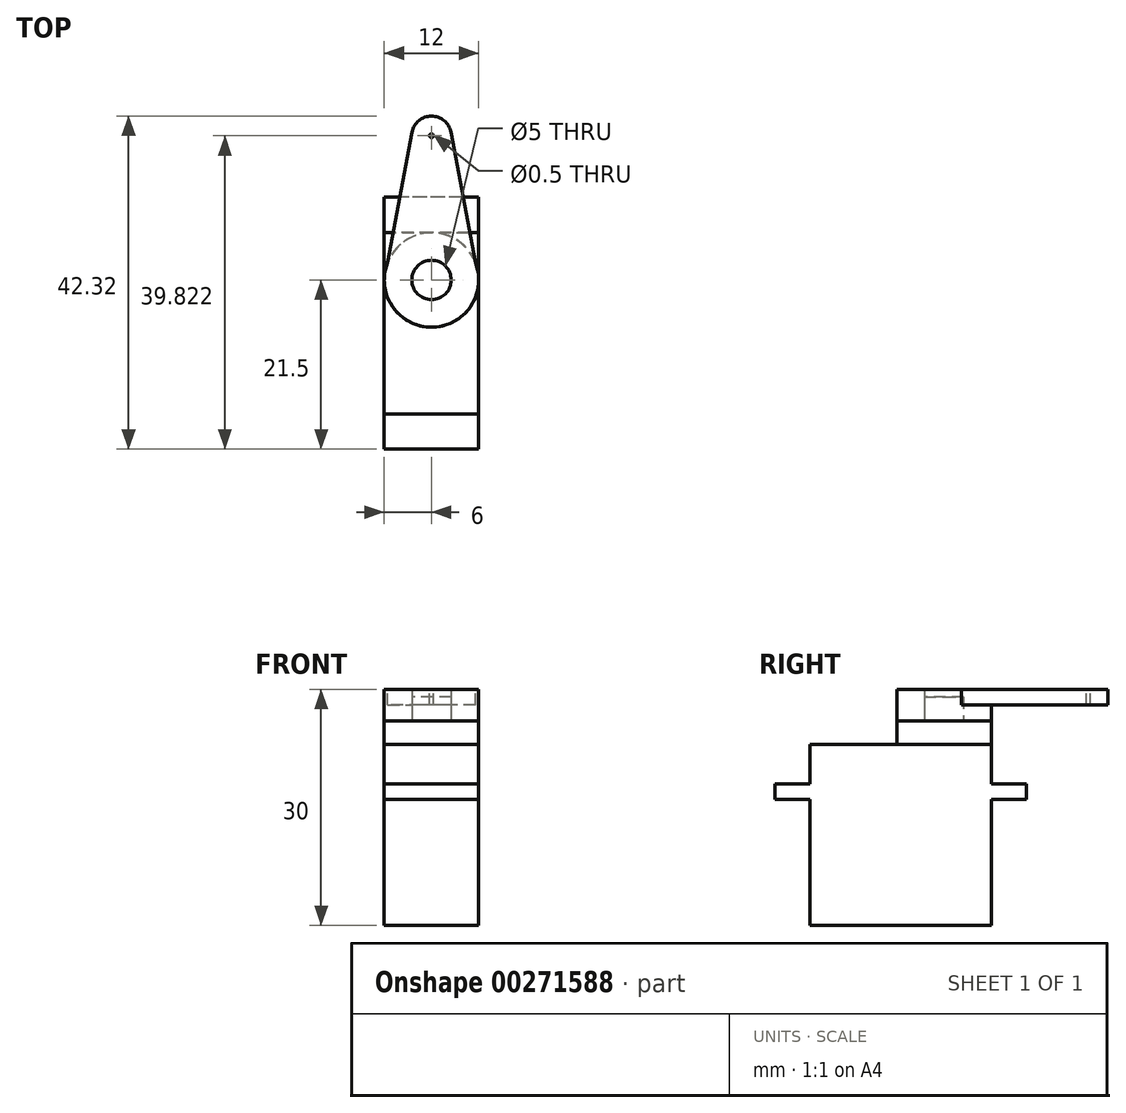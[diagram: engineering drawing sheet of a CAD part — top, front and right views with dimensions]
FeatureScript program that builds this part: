
annotation { "Feature Type Name" : "Feature", "Feature Type Description" : "" }
export const myFeature = defineFeature(function(context is Context, id is Id, definition is map)
    precondition{}
    {
        {
            var Q0;
            Q0=qCreatedBy(makeId("Top.planeOp"),FACE);
            var sketch = newSketch(context, id + "F0", { "sketchPlane" : qUnion([Q0])});
            skLineSegment(sketch, "E0.bottom", {"start": v(6, -16) * mm, "end": v(-6, -16) * mm});
            skLineSegment(sketch, "E0.top", {"start": v(6, 16) * mm, "end": v(-6, 16) * mm});
            skLineSegment(sketch, "E0.left", {"start": v(6, -16) * mm, "end": v(6, 16) * mm});
            skLineSegment(sketch, "E0.right", {"start": v(-6, -16) * mm, "end": v(-6, 16) * mm});
            skPoint(sketch, "E0.middle", {"position": v(0, 0) * mm});
            skSolve(sketch);
        }
        {
            var Q0;
            Q0 = qSketchRegion(id + "F0", true);
            extrude(context, id + "F1", {"entities" : qUnion([Q0]), "depth" : 2 * mm});
        }
        {
            var Q0;
            Q0=makeQuery(id+"F1.opExtrude","CAP_FACE",FACE,{"disambiguationData":[OSD([sQuery(id+"F0.wireOp",EDGE,"E0.bottom"),sQuery(id+"F0.wireOp",EDGE,"E0.top"),sQuery(id+"F0.wireOp",EDGE,"E0.left"),sQuery(id+"F0.wireOp",EDGE,"E0.right")])],"isStart":false});
            var sketch = newSketch(context, id + "F2", { "sketchPlane" : qUnion([Q0])});
            skLineSegment(sketch, "E1.bottom", {"start": v(6, -11.5) * mm, "end": v(-6, -11.5) * mm});
            skLineSegment(sketch, "E1.top", {"start": v(6, 11.5) * mm, "end": v(-6, 11.5) * mm});
            skLineSegment(sketch, "E1.left", {"start": v(6, -11.5) * mm, "end": v(6, 11.5) * mm});
            skLineSegment(sketch, "E1.right", {"start": v(-6, -11.5) * mm, "end": v(-6, 11.5) * mm});
            skPoint(sketch, "E1.middle", {"position": v(0, 0) * mm});
            skSolve(sketch);
        }
        {
            var Q0;
            Q0 = qSketchRegion(id + "F2", true);
            extrude(context, id + "F3", {"entities" : qUnion([Q0]), "operationType" : NewBodyOperationType.ADD, "depth" : 5 * mm, "hasSecondDirection" : true, "secondDirectionOppositeDirection" : true, "secondDirectionDepth" : 18 * mm});
        }
        {
            var Q0;
            Q0=makeQuery(id+"F3.opExtrude","CAP_FACE",FACE,{"disambiguationData":[OSD([sQuery(id+"F2.wireOp",EDGE,"E1.bottom"),sQuery(id+"F2.wireOp",EDGE,"E1.top"),sQuery(id+"F2.wireOp",EDGE,"E1.left"),sQuery(id+"F2.wireOp",EDGE,"E1.right")])],"isStart":false});
            var sketch = newSketch(context, id + "F4", { "sketchPlane" : qUnion([Q0])});
            skCircle(sketch, "E2", {"center": v(0, 5.5) * mm, "radius": 6 * mm});
            skPoint(sketch, "E3", {"position": v(0, 11.5) * mm});
            skSolve(sketch);
        }
        {
            var Q0;
            {var subQ0=sQuery(id+"F4.wireOp",EDGE,"E2");var subQ1=makeQuery(id+"F4.imprint","INTERSECT",VERTEX,{"derivedFrom":[makeQuery(id+"F3.opExtrude","CAP_EDGE",EDGE,{"disambiguationData":[OSD([sQuery(id+"F2.wireOp",EDGE,"E1.top")])],"isStart":false}),subQ0]});Q0=makeQuery(id+"F4.imprint","IMPRINT",FACE,{"disambiguationData":[TD([[makeQuery(id+"F4.imprint","IMPRINT",EDGE,{"disambiguationData":[TD([[subQ1,1.0]])],"derivedFrom":subQ0}),1.0]])]});}
            extrude(context, id + "F5", {"entities" : qUnion([Q0]), "operationType" : NewBodyOperationType.ADD, "depth" : 3 * mm});
        }
        {
            var Q0;
            Q0=makeQuery(id+"F5.opExtrude","CAP_FACE",FACE,{"disambiguationData":[OSD([sQuery(id+"F4.wireOp",EDGE,"E2")])],"isStart":false});
            var sketch = newSketch(context, id + "F6", { "sketchPlane" : qUnion([Q0])});
            skCircle(sketch, "E4", {"center": v(0, 5.5) * mm, "radius": 2.5 * mm});
            skSolve(sketch);
        }
        {
            var Q0;
            Q0 = qSketchRegion(id + "F6", true);
            extrude(context, id + "F7", {"entities" : qUnion([Q0]), "operationType" : NewBodyOperationType.ADD, "depth" : 3 * mm});
        }
        {
            var Q0;
            Q0=makeQuery(id+"F5.opExtrude","CAP_FACE",FACE,{"disambiguationData":[OSD([sQuery(id+"F4.wireOp",EDGE,"E2")])],"isStart":false});
            extrude(context, id + "F8", {"entities" : qUnion([Q0]), "depth" : 4 * mm});
        }
        {
            var Q0;
            Q0=makeQuery(id+"F8.opExtrude","CAP_FACE",FACE,{"disambiguationData":[OSD([sQuery(id+"F4.wireOp",EDGE,"E2")])],"isStart":false});
            var sketch = newSketch(context, id + "F9", { "sketchPlane" : qUnion([Q0])});
            skPoint(sketch, "E5", {"position": v(0, 5.5) * mm});
            skLineSegment(sketch, "E6", {"start": v(-6, 5.5) * mm, "end": v(-2.45, 24.32) * mm});
            skLineSegment(sketch, "E7", {"start": v(6, 5.5) * mm, "end": v(2.44, 24.36) * mm});
            skArc(sketch, "E8", {"start": v(2.46, 24.29) * mm, "mid": v(0, 26.32) * mm, "end": v(-2.46, 24.29) * mm});
            skPoint(sketch, "E8.third.point", {"position": v(0.08, 26.32) * mm});
            skCircle(sketch, "E9", {"center": v(0, 23.82) * mm, "radius": 0.25 * mm});
            skSolve(sketch);
        }
        {
            var Q0;
            {var subQ0=sQuery(id+"F9.wireOp",EDGE,"E8");Q0=makeQuery(id+"F9.imprint","IMPRINT",FACE,{"disambiguationData":[TD([[makeQuery(id+"F9.imprint","IMPRINT",EDGE,{"derivedFrom":subQ0}),1.0]])]});}
            extrude(context, id + "F10", {"entities" : qUnion([Q0]), "operationType" : NewBodyOperationType.ADD, "oppositeDirection" : true, "depth" : 2 * mm});
        }
    });
